# Revit family: SDP-825
name_source: partatom
category: Устройства связи
revit_build: Autodesk Revit 2017 (Build: 20170118_1100(x64)
units: mm (PartAtom-declared; Revit-internal decimal feet)

## family parameters
Всегда вертикально = Нет
На основе рабочей плоскости = Нет
Общий = Нет
При загрузке вырезать с полостями = Нет
Размер круглого соединителя = Использовать диаметр
Сохранять ориентацию аннотаций = Нет
Тип детали = Нормальный
Точка расчета площади = Нет

## types (1)
- SDP-825 IP-видеокамера
    ADSK_URL страницы изделия = https://stilsoft.ru
    ADSK_Единица измерения = шт.
    ADSK_Завод-изготовитель = ООО «Основа Безопасности»
    ADSK_Количество = 1
    ADSK_Марка = СТВФ.426459.009-03
    ADSK_Масса = 3
    ADSK_Наименование = IP-видеокамера SDP-825
    ADSK_Размер_Высота = 320 мм
    ADSK_Размер_ДиаметрИзделия = 220 мм
    d_короба = 20 мм
    Баланс белого = Авто / Ручной
    Диапазон наклона, до, град. = 5-90 автопереворот изображения
    Диапазон поворота, до, град. = 360 без ограничений
    Количество предустановок, шт. = 300
    Количество режимов обхода, шт = 4 (до 10 минут)
    Компенсация засветки = BLC, HLC, D-WDR
    Матрица = 1/2.8’’ Sony CMOS
    Мощность = 27
    Напряжение = 24
    Поддерживаемые протоколы = Onvif, GB28181, HTTP, RTSP, RTP, TCP, UDP
    Разрешение при скорости 25 к/сек, пикс. = 1920х1080
    Режим «день/ночь» = Авто / Ручной
    Сеть = 10/100 Base-T/TX, RJ45, IEEE 802.3
    Система шумоподавления = 3D-DNR
    Скорость наклона, до, град/сек = 200
    Скорость поворота, до, град/сек = 300
    Тип объектива = Встроенный трансфокатор с автофокусировкой
    Увеличение оптическое = 30х
    Увеличение цифровое = 4х
    Угол зрения по горизонтали, град. = 60,5 – 2,3
    Управление = Веб-интерфейс
    Фокусное расстояние, мм = 4.7-141 (F1,5-4)
    Формат сжатия = H.265, Н.264, MJPEG
    Чувствительность цвет, Люкс = 0,005 (F1,5)
    Чувствительность ч/б, Люкс = 0,0005 (F1,5)
